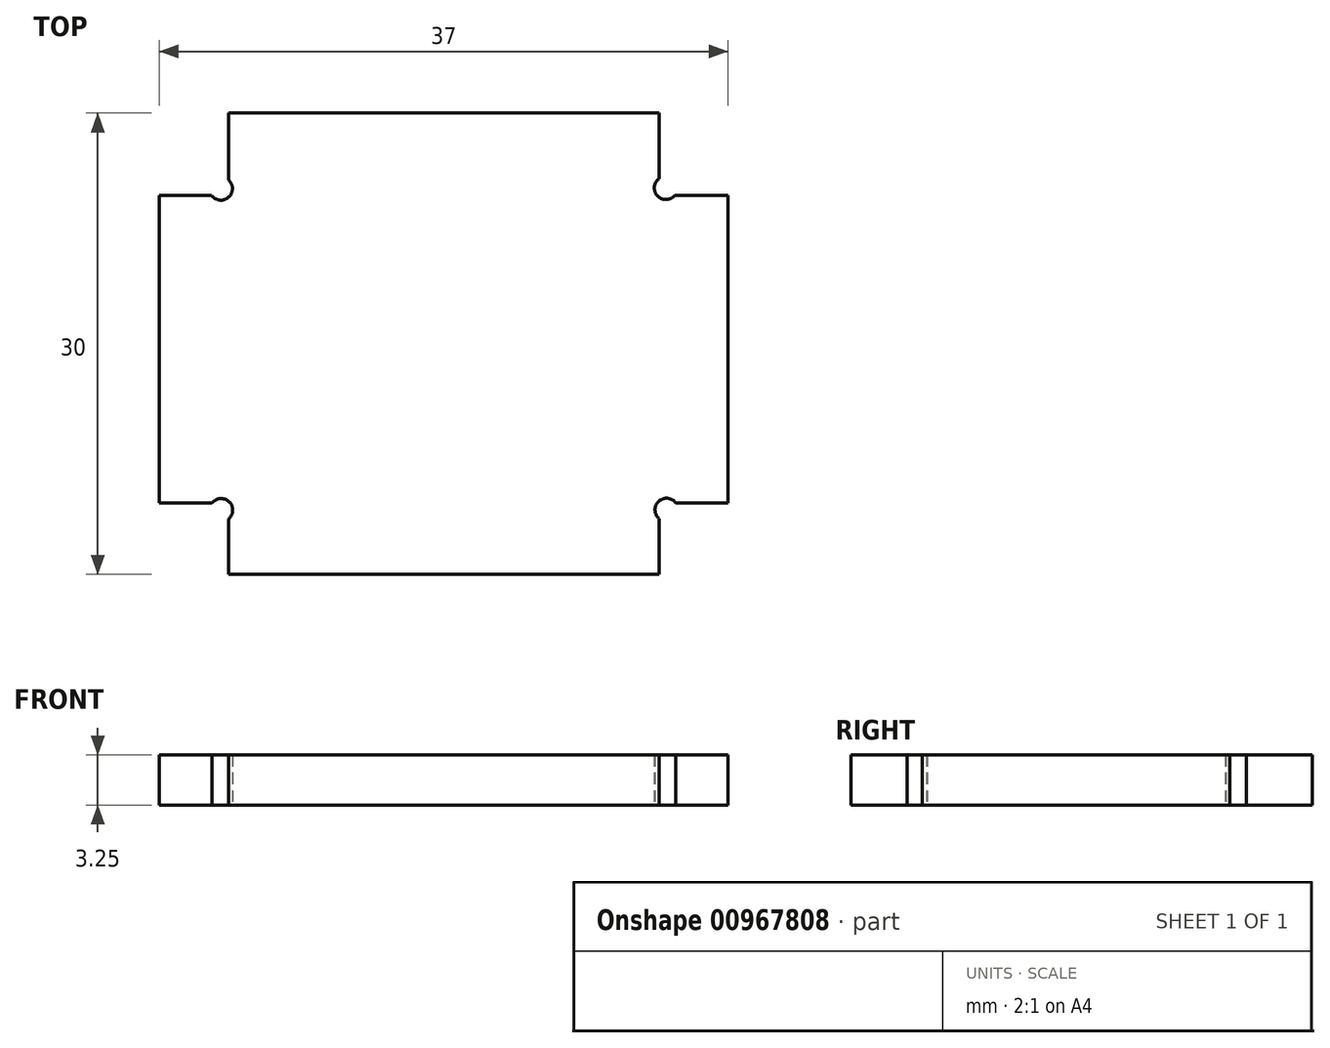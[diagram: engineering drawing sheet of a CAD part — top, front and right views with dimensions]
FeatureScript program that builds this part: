
annotation { "Feature Type Name" : "Feature", "Feature Type Description" : "" }
export const myFeature = defineFeature(function(context is Context, id is Id, definition is map)
    precondition{}
    {
        {
            var Q0;
            Q0=qCreatedBy(makeId("Top.planeOp"),FACE);
            var sketch = newSketch(context, id + "F0", { "sketchPlane" : qUnion([Q0])});
            skLineSegment(sketch, "E0.right", {"start": v(-18.5, 9.63) * mm, "end": v(-18.5, -10.37) * mm});
            skPoint(sketch, "E0.middle", {"position": v(0, 0) * mm});
            skLineSegment(sketch, "E1.bottom", {"start": v(14, -15) * mm, "end": v(-14, -15) * mm});
            skLineSegment(sketch, "E1.top", {"start": v(14, 15) * mm, "end": v(-14, 15) * mm});
            skPoint(sketch, "E2", {"position": v(-14, 9.63) * mm});
            skPoint(sketch, "E3", {"position": v(-14, 15) * mm});
            skPoint(sketch, "E4", {"position": v(-18.5, 9.63) * mm});
            skPoint(sketch, "E5", {"position": v(-18.5, -10.37) * mm});
            skPoint(sketch, "E6", {"position": v(-14, -10.37) * mm});
            skPoint(sketch, "E7", {"position": v(-14, -15) * mm});
            skPoint(sketch, "E8", {"position": v(14, -15) * mm});
            skPoint(sketch, "E9", {"position": v(14, -10.37) * mm});
            skPoint(sketch, "E10", {"position": v(14, 15) * mm});
            skLineSegment(sketch, "E11", {"start": v(-18.5, 9.63) * mm, "end": v(-14, 9.63) * mm});
            skLineSegment(sketch, "E12", {"start": v(-14, 9.63) * mm, "end": v(-14, 15) * mm});
            skLineSegment(sketch, "E13", {"start": v(14, -10.37) * mm, "end": v(14, -15) * mm});
            skLineSegment(sketch, "E14", {"start": v(-14, -15) * mm, "end": v(-14, -10.37) * mm});
            skLineSegment(sketch, "E15", {"start": v(-14, -10.37) * mm, "end": v(-18.5, -10.37) * mm});
            skCircle(sketch, "E16", {"center": v(14.5, -10.8) * mm, "radius": 0.75 * mm});
            skCircle(sketch, "E17", {"center": v(14.45, 10.13) * mm, "radius": 0.75 * mm});
            skCircle(sketch, "E18", {"center": v(-14.49, 10.08) * mm, "radius": 0.75 * mm});
            skCircle(sketch, "E19", {"center": v(-14.47, -10.82) * mm, "radius": 0.75 * mm});
            skPoint(sketch, "E20", {"position": v(14, 9.64) * mm});
            skPoint(sketch, "E21", {"position": v(18.5, 9.63) * mm});
            skPoint(sketch, "E22", {"position": v(18.5, -10.37) * mm});
            skLineSegment(sketch, "E23", {"start": v(14, 15) * mm, "end": v(14, 9.64) * mm});
            skLineSegment(sketch, "E24", {"start": v(18.5, 9.63) * mm, "end": v(14, 9.64) * mm});
            skLineSegment(sketch, "E25", {"start": v(18.5, 9.63) * mm, "end": v(18.5, -10.37) * mm});
            skLineSegment(sketch, "E26", {"start": v(18.5, -10.37) * mm, "end": v(14, -10.37) * mm});
            skSolve(sketch);
        }
        {
            var Q0;
            {var subQ20=sQuery(id+"F0.wireOp",EDGE,"E0.left");Q0=makeQuery(id+"F0.imprint","IMPRINT",FACE,{"disambiguationData":[TD([[makeQuery(id+"F0.imprint","IMPRINT",EDGE,{"derivedFrom":subQ20}),-1.0]])]});}
            var Q1;
            {var subQ16=sQuery(id+"F0.wireOp",EDGE,"E0.right");Q1=makeQuery(id+"F0.imprint","IMPRINT",FACE,{"disambiguationData":[TD([[makeQuery(id+"F0.imprint","IMPRINT",EDGE,{"derivedFrom":subQ16}),1.0]])]});}
            extrude(context, id + "F1", {"entities" : qUnion([Q0, Q1]), "depth" : 3.25 * mm, "offsetDistance" : 25 * mm});
        }
    });
